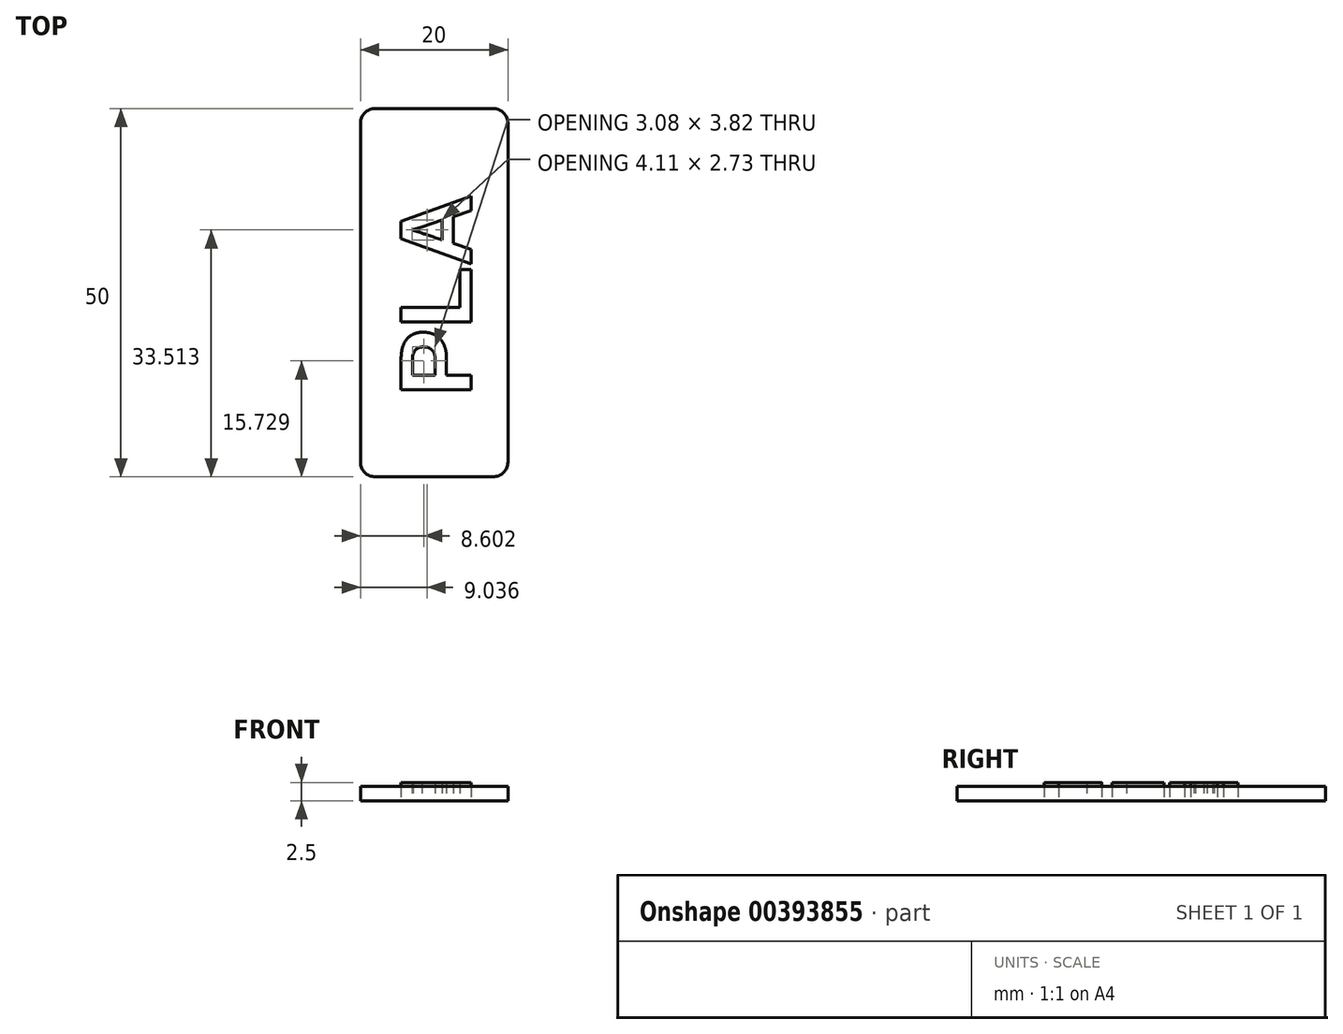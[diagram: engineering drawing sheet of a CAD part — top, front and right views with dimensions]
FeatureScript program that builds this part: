
annotation { "Feature Type Name" : "Feature", "Feature Type Description" : "" }
export const myFeature = defineFeature(function(context is Context, id is Id, definition is map)
    precondition{}
    {
        {
            var Q0;
            Q0=qCreatedBy(makeId("Top.planeOp"),FACE);
            var sketch = newSketch(context, id + "F0", { "sketchPlane" : qUnion([Q0])});
            skLineSegment(sketch, "E0.bottom", {"start": v(-20, -25) * mm, "end": v(0, -25) * mm});
            skLineSegment(sketch, "E0.top", {"start": v(-20, 25) * mm, "end": v(0, 25) * mm});
            skLineSegment(sketch, "E0.left", {"start": v(-20, -25) * mm, "end": v(-20, 25) * mm});
            skLineSegment(sketch, "E0.right", {"start": v(0, -25) * mm, "end": v(0, 25) * mm});
            skSolve(sketch);
        }
        {
            var Q0;
            Q0=makeQuery(id+"F0.imprint","IMPRINT",FACE,{"disambiguationData":[TD([[makeQuery(id+"F0.imprint","IMPRINT",EDGE,{"derivedFrom":sQuery(id+"F0.wireOp",EDGE,"E0.bottom")}),1.0]])]});
            extrude(context, id + "F1", {"entities" : qUnion([Q0]), "depth" : 2 * mm});
        }
        {
            var Q0;
            Q0=makeQuery(id+"F1.opExtrude","SWEPT_EDGE",EDGE,{"disambiguationData":[OSD([sQuery(id+"F0.wireOp",EDGE,"E0.bottom"),sQuery(id+"F0.wireOp",EDGE,"E0.right")])]});
            var Q1;
            Q1=makeQuery(id+"F1.opExtrude","SWEPT_EDGE",EDGE,{"disambiguationData":[OSD([sQuery(id+"F0.wireOp",EDGE,"E0.bottom"),sQuery(id+"F0.wireOp",EDGE,"E0.left")])]});
            var Q2;
            Q2=makeQuery(id+"F1.opExtrude","SWEPT_EDGE",EDGE,{"disambiguationData":[OSD([sQuery(id+"F0.wireOp",EDGE,"E0.top"),sQuery(id+"F0.wireOp",EDGE,"E0.right")])]});
            var Q3;
            Q3=makeQuery(id+"F1.opExtrude","SWEPT_EDGE",EDGE,{"disambiguationData":[OSD([sQuery(id+"F0.wireOp",EDGE,"E0.top"),sQuery(id+"F0.wireOp",EDGE,"E0.left")])]});
            fillet(context, id + "F2", {"entities" : qUnion([Q0, Q1, Q2, Q3]), "radius" : 2 * mm, "tangentPropagation" : true, "allowEdgeOverflow" : false});
        }
        {
            var Q0;
            Q0=qCreatedBy(makeId("Top.planeOp"),FACE);
            var sketch = newSketch(context, id + "F3", { "sketchPlane" : qUnion([Q0])});
            skText(sketch, "E1", { "text": "PLA", "fontName": "Arimo-Bold.ttf"});
            const initialGuessF3  = {"E1": [-0.00499, -0.01409, 0, 1, 0.00993]};
            skSetInitialGuess(sketch, initialGuessF3);
            skSolve(sketch);
        }
        {
            var Q0;
            Q0=qSketchRegion(id+"F3",true);
            extrude(context, id + "F4", {"entities" : qUnion([Q0]), "depth" : 2.5 * mm});
        }
    });
